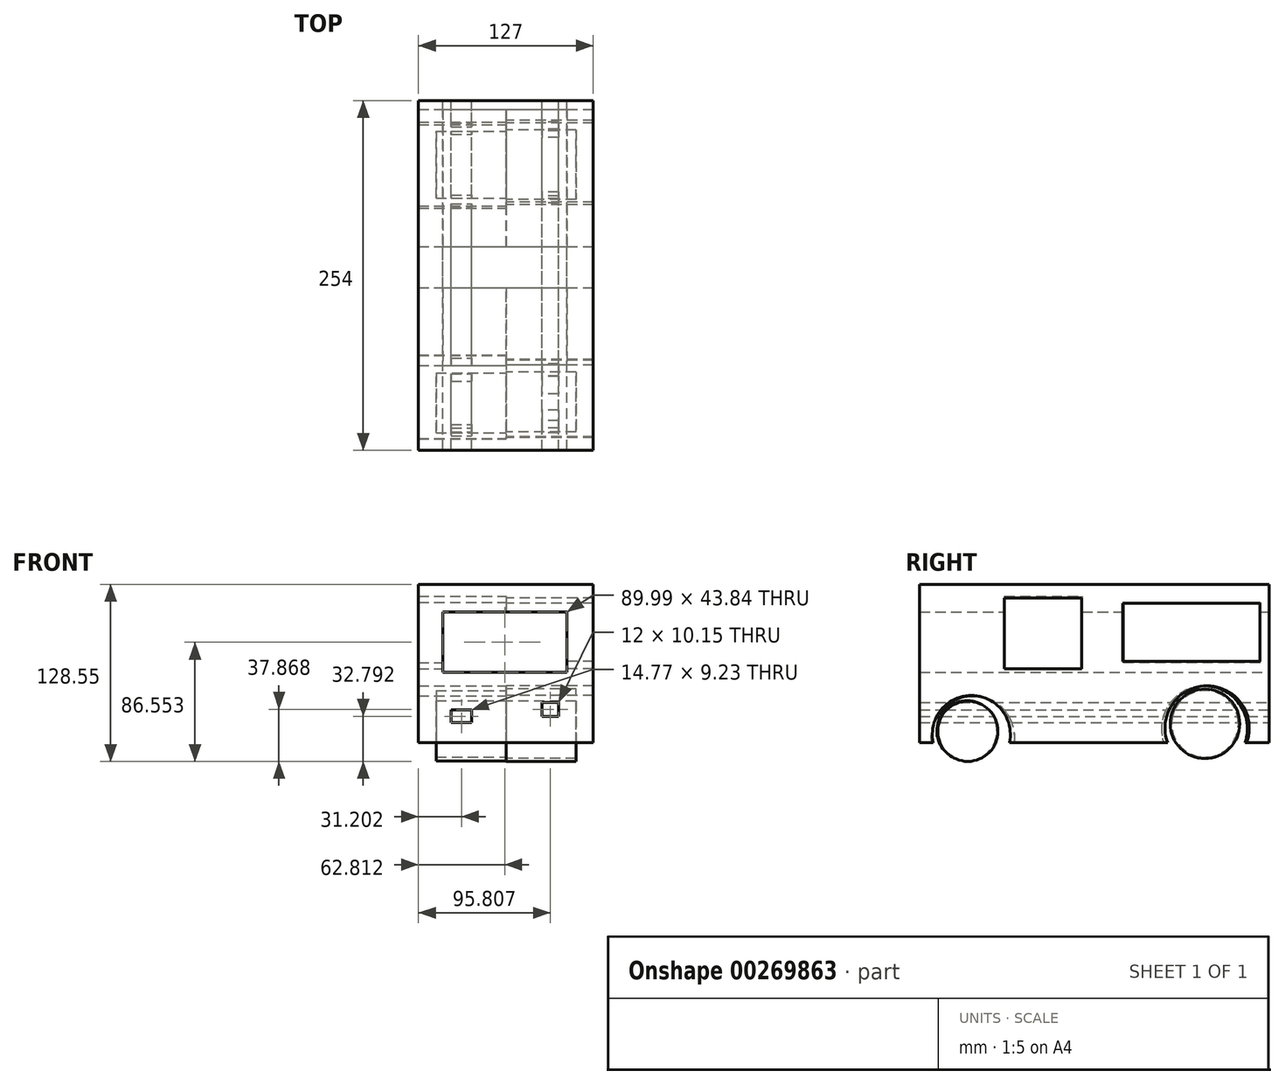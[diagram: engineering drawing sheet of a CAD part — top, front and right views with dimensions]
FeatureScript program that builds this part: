
annotation { "Feature Type Name" : "Feature", "Feature Type Description" : "" }
export const myFeature = defineFeature(function(context is Context, id is Id, definition is map)
    precondition{}
    {
        {
            var Q0;
            Q0=qCreatedBy(makeId("Front.planeOp"),FACE);
            var sketch = newSketch(context, id + "F0", { "sketchPlane" : qUnion([Q0])});
            skLineSegment(sketch, "E0.bottom", {"start": v(-63.69, 46.5) * mm, "end": v(63.31, 46.5) * mm});
            skLineSegment(sketch, "E0.top", {"start": v(-63.69, -68.4) * mm, "end": v(63.31, -68.4) * mm});
            skLineSegment(sketch, "E0.left", {"start": v(-63.69, 46.5) * mm, "end": v(-63.69, -68.4) * mm});
            skLineSegment(sketch, "E0.right", {"start": v(63.31, 46.5) * mm, "end": v(63.31, -68.4) * mm});
            skSolve(sketch);
        }
        {
            var Q0;
            Q0 = qSketchRegion(id + "F0", true);
            extrude(context, id + "F1", {"entities" : qUnion([Q0]), "depth" : 254 * mm});
        }
        {
            var Q0;
            Q0=qCreatedBy(makeId("Right.planeOp"),FACE);
            var sketch = newSketch(context, id + "F2", { "sketchPlane" : qUnion([Q0])});
            skLineSegment(sketch, "E1", {"start": v(-200.64, 45.63) * mm, "end": v(-255.25, -14.7) * mm});
            skLineSegment(sketch, "E2.bottom", {"start": v(-192.39, 38) * mm, "end": v(-135.87, 38) * mm});
            skLineSegment(sketch, "E2.top", {"start": v(-192.39, -14.7) * mm, "end": v(-135.87, -14.7) * mm});
            skLineSegment(sketch, "E2.left", {"start": v(-192.39, 38) * mm, "end": v(-192.39, -14.7) * mm});
            skLineSegment(sketch, "E2.right", {"start": v(-135.87, 38) * mm, "end": v(-135.87, -14.7) * mm});
            skLineSegment(sketch, "E3.bottom", {"start": v(-106.03, 33.56) * mm, "end": v(-6.34, 33.56) * mm});
            skLineSegment(sketch, "E3.top", {"start": v(-106.03, -10.25) * mm, "end": v(-6.34, -10.25) * mm});
            skLineSegment(sketch, "E3.left", {"start": v(-106.03, 33.56) * mm, "end": v(-106.03, -10.25) * mm});
            skLineSegment(sketch, "E3.right", {"start": v(-6.34, 33.56) * mm, "end": v(-6.34, -10.25) * mm});
            skCircle(sketch, "E4", {"center": v(-215.25, -64.86) * mm, "radius": 30.4 * mm});
            skCircle(sketch, "E5", {"center": v(-46.98, -58.51) * mm, "radius": 31.24 * mm});
            skSolve(sketch);
        }
        {
            var Q0;
            Q0 = qSketchRegion(id + "F2", true);
            extrude(context, id + "F3", {"entities" : qUnion([Q0]), "operationType" : NewBodyOperationType.REMOVE, "oppositeDirection" : true, "depth" : 127 * mm});
        }
        {
            var Q0;
            Q0=qCreatedBy(makeId("Right.planeOp"),FACE);
            var sketch = newSketch(context, id + "F4", { "sketchPlane" : qUnion([Q0])});
            skLineSegment(sketch, "E6.bottom", {"start": v(-6.64, 32.97) * mm, "end": v(-106.24, 32.97) * mm});
            skLineSegment(sketch, "E6.top", {"start": v(-6.64, -9.52) * mm, "end": v(-106.24, -9.52) * mm});
            skLineSegment(sketch, "E6.left", {"start": v(-6.64, 32.97) * mm, "end": v(-6.64, -9.52) * mm});
            skLineSegment(sketch, "E6.right", {"start": v(-106.24, 32.97) * mm, "end": v(-106.24, -9.52) * mm});
            skLineSegment(sketch, "E7.bottom", {"start": v(-136.15, 36.71) * mm, "end": v(-192.23, 36.71) * mm});
            skLineSegment(sketch, "E7.top", {"start": v(-136.15, -14.62) * mm, "end": v(-192.23, -14.62) * mm});
            skLineSegment(sketch, "E7.left", {"start": v(-136.15, 36.71) * mm, "end": v(-136.15, -14.62) * mm});
            skLineSegment(sketch, "E7.right", {"start": v(-192.23, 36.71) * mm, "end": v(-192.23, -14.62) * mm});
            skCircle(sketch, "E8", {"center": v(-45.05, -57.79) * mm, "radius": 30.6 * mm});
            skCircle(sketch, "E9", {"center": v(-216.37, -62.54) * mm, "radius": 28.37 * mm});
            skSolve(sketch);
        }
        {
            var Q0;
            Q0 = qSketchRegion(id + "F4", true);
            extrude(context, id + "F5", {"entities" : qUnion([Q0]), "operationType" : NewBodyOperationType.REMOVE, "depth" : 127 * mm});
        }
        {
            var Q0;
            Q0=qCreatedBy(makeId("Right.planeOp"),FACE);
            var sketch = newSketch(context, id + "F6", { "sketchPlane" : qUnion([Q0])});
            skCircle(sketch, "E10", {"center": v(-218.91, -60.16) * mm, "radius": 21.87 * mm});
            skCircle(sketch, "E11", {"center": v(-46.58, -54.73) * mm, "radius": 25.24 * mm});
            skSolve(sketch);
        }
        {
            var Q0;
            Q0 = qSketchRegion(id + "F6", true);
            extrude(context, id + "F7", {"entities" : qUnion([Q0]), "depth" : 50.8 * mm});
        }
        {
            var Q0;
            Q0=makeQuery(id+"F7.opExtrude","CAP_FACE",FACE,{"disambiguationData":[OSD([sQuery(id+"F6.wireOp",EDGE,"E11")])],"isStart":true});
            var sketch = newSketch(context, id + "F8", { "sketchPlane" : qUnion([Q0])});
            skCircle(sketch, "E12", {"center": v(46.58, -54.73) * mm, "radius": 24.22 * mm});
            skCircle(sketch, "E13", {"center": v(219.55, -59.8) * mm, "radius": 21.86 * mm});
            skSolve(sketch);
        }
        {
            var Q0;
            Q0 = qSketchRegion(id + "F8", true);
            extrude(context, id + "F9", {"entities" : qUnion([Q0]), "depth" : 50.8 * mm});
        }
        {
            var Q0;
            Q0=qCreatedBy(makeId("Front.planeOp"),FACE);
            var sketch = newSketch(context, id + "F10", { "sketchPlane" : qUnion([Q0])});
            skLineSegment(sketch, "E14.bottom", {"start": v(44.12, 26.43) * mm, "end": v(-45.87, 26.43) * mm});
            skLineSegment(sketch, "E14.top", {"start": v(44.12, -17.4) * mm, "end": v(-45.87, -17.4) * mm});
            skLineSegment(sketch, "E14.left", {"start": v(44.12, 26.43) * mm, "end": v(44.12, -17.4) * mm});
            skLineSegment(sketch, "E14.right", {"start": v(-45.87, 26.43) * mm, "end": v(-45.87, -17.4) * mm});
            skLineSegment(sketch, "E15.bottom", {"start": v(38.12, -39.1) * mm, "end": v(26.12, -39.1) * mm});
            skLineSegment(sketch, "E15.top", {"start": v(38.12, -49.25) * mm, "end": v(26.12, -49.25) * mm});
            skLineSegment(sketch, "E15.left", {"start": v(38.12, -39.1) * mm, "end": v(38.12, -49.25) * mm});
            skLineSegment(sketch, "E15.right", {"start": v(26.12, -39.1) * mm, "end": v(26.12, -49.25) * mm});
            skLineSegment(sketch, "E16.bottom", {"start": v(-25.1, -44.63) * mm, "end": v(-39.87, -44.63) * mm});
            skLineSegment(sketch, "E16.top", {"start": v(-25.1, -53.86) * mm, "end": v(-39.87, -53.86) * mm});
            skLineSegment(sketch, "E16.left", {"start": v(-25.1, -44.63) * mm, "end": v(-25.1, -53.86) * mm});
            skLineSegment(sketch, "E16.right", {"start": v(-39.87, -44.63) * mm, "end": v(-39.87, -53.86) * mm});
            skSolve(sketch);
        }
        {
            var Q0;
            Q0 = qSketchRegion(id + "F10", true);
            extrude(context, id + "F11", {"entities" : qUnion([Q0]), "operationType" : NewBodyOperationType.REMOVE, "depth" : 254 * mm});
        }
    });
